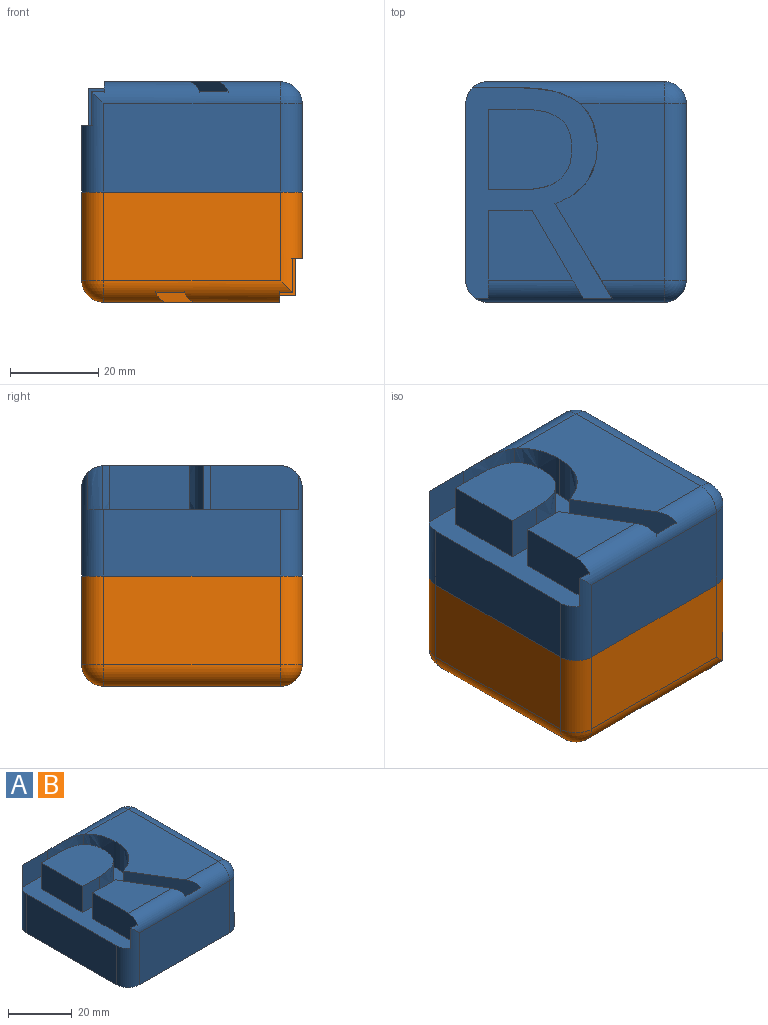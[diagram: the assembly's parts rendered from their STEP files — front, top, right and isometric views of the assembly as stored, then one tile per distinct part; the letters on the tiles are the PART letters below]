
ASSEMBLY  parts=2 mates=1
PART A: 35 faces, bbox 50x50x25 mm
  f0: plane 19.12x15.73mm, normal (0,0,1), area 228.6mm2, adj f16,f17,f18,f28
  f1: plane 40x15mm, normal (-1,0,0), area 600mm2, adj f6,f9,f26,f34
  f2: plane 40.23x24.79mm, normal (0,0,1), area 725.2mm2, adj f20,f21,f22,f28,f31,f33
  f3: plane 40x20mm, normal (0,1,0), area 800mm2, adj f6,f30,f33,f34
  f4: plane 40x20mm, normal (0,-1,0), area 800mm2, adj f6,f26,f27,f28
  f5: plane 40x20mm, normal (1,0,0), area 800mm2, adj f6,f27,f30,f31
  f6: plane 50x50mm, normal (0,0,-1), area 2478.5mm2, adj f1,f3,f4,f5,f26,f27,f30,f34
  f7: plane 7.85x2.95mm, normal (0,1,0), area 23.2mm2, adj f9,f16,f26,f28
  f8: plane 11.12x8.48mm, normal (0,-1,0), area 94.3mm2, adj f9,f23,f33,f34
  f9: plane 47.7x33.17mm, normal (0,0,1), area 657.1mm2, adj f1,f7,f8,f10,f11,f12,f13,f14
  f10: plane 10x7.61mm, normal (0,-1,0), area 76.1mm2, adj f9,f11,f24,f25
  f11: plane 18.24x10mm, normal (-1,0,0), area 182.4mm2, adj f9,f10,f12,f25
  f12: plane 10x7.21mm, normal (0,1,0), area 72.1mm2, adj f9,f11,f13,f25
  f13: extruded ~10x8.96mm, area 93.5mm2, adj f9,f12,f14,f25
  f14: extruded ~10x6.82mm, area 76.5mm2, adj f9,f13,f15,f25
  f15: extruded ~10x7mm, area 77.7mm2, adj f9,f14,f24,f25
  f16: plane 19.84x10mm, normal (-1,0,0), area 195.7mm2, adj f0,f7,f9,f17,f28
  f17: plane 10x9.96mm, normal (0,1,0), area 99.6mm2, adj f0,f9,f16,f18
  f18: plane 19.84x11.55mm, normal (0.86,0.5,0), area 226.5mm2, adj f0,f9,f17,f19,f28
  f19: plane 7.85x6.56mm, normal (0,1,0), area 51.5mm2, adj f9,f18,f20,f28
  f20: plane 21.43x12.96mm, normal (-0.86,-0.52,0), area 247.4mm2, adj f2,f9,f19,f21,f28
  f21: extruded ~12.79x10mm, area 172.5mm2, adj f2,f9,f20,f22
  f22: extruded ~10.12x10mm, area 113.5mm2, adj f2,f9,f21,f23,f33
  f23: extruded ~12.97x9.99mm, area 124.5mm2, adj f8,f9,f22,f33
  f24: extruded ~10x8.61mm, area 91mm2, adj f9,f10,f15,f25
  f25: plane 18.96x18.24mm, normal (0,0,1), area 312.6mm2, adj f10,f11,f12,f13,f14,f15,f24
  f26: cylinder r=5mm len=22.85mm, axis (0,0,-1), area 137.4mm2, adj f1,f4,f6,f7,f9,f28
  f27: cylinder r=5mm len=20mm, axis (0,0,1), area 157.1mm2, adj f4,f5,f6,f29
  f28: cylinder r=5mm len=42.85mm, axis (-1,0,0), area 286.7mm2, adj f0,f2,f4,f7,f16,f18,f19,f20
  f29: sphere r=5mm, area 39.3mm2, adj f27,f28,f31
  f30: cylinder r=5mm len=20mm, axis (0,0,-1), area 157.1mm2, adj f3,f5,f6,f32
  f31: cylinder r=5mm len=40mm, axis (0,-1,0), area 314.2mm2, adj f2,f5,f29,f32
  f32: sphere r=5mm, area 39.3mm2, adj f30,f31,f33
  f33: cylinder r=5mm len=43.48mm, axis (1,0,0), area 253.1mm2, adj f2,f3,f8,f22,f23,f32,f34
  f34: cylinder r=5mm len=23.48mm, axis (0,0,1), area 144.1mm2, adj f1,f3,f6,f8,f9,f33
PART B: same geometry as A
PLACE A t=(-136.12,48.79,8.98)mm
PLACE B rot(axis=(0,1,0),180deg) t=(-137.73,48.79,8.98)mm
MATE parallel B.f6 <-> A.f6  axis (0,0,1) through (-136.92,46.02,8.98)mm
